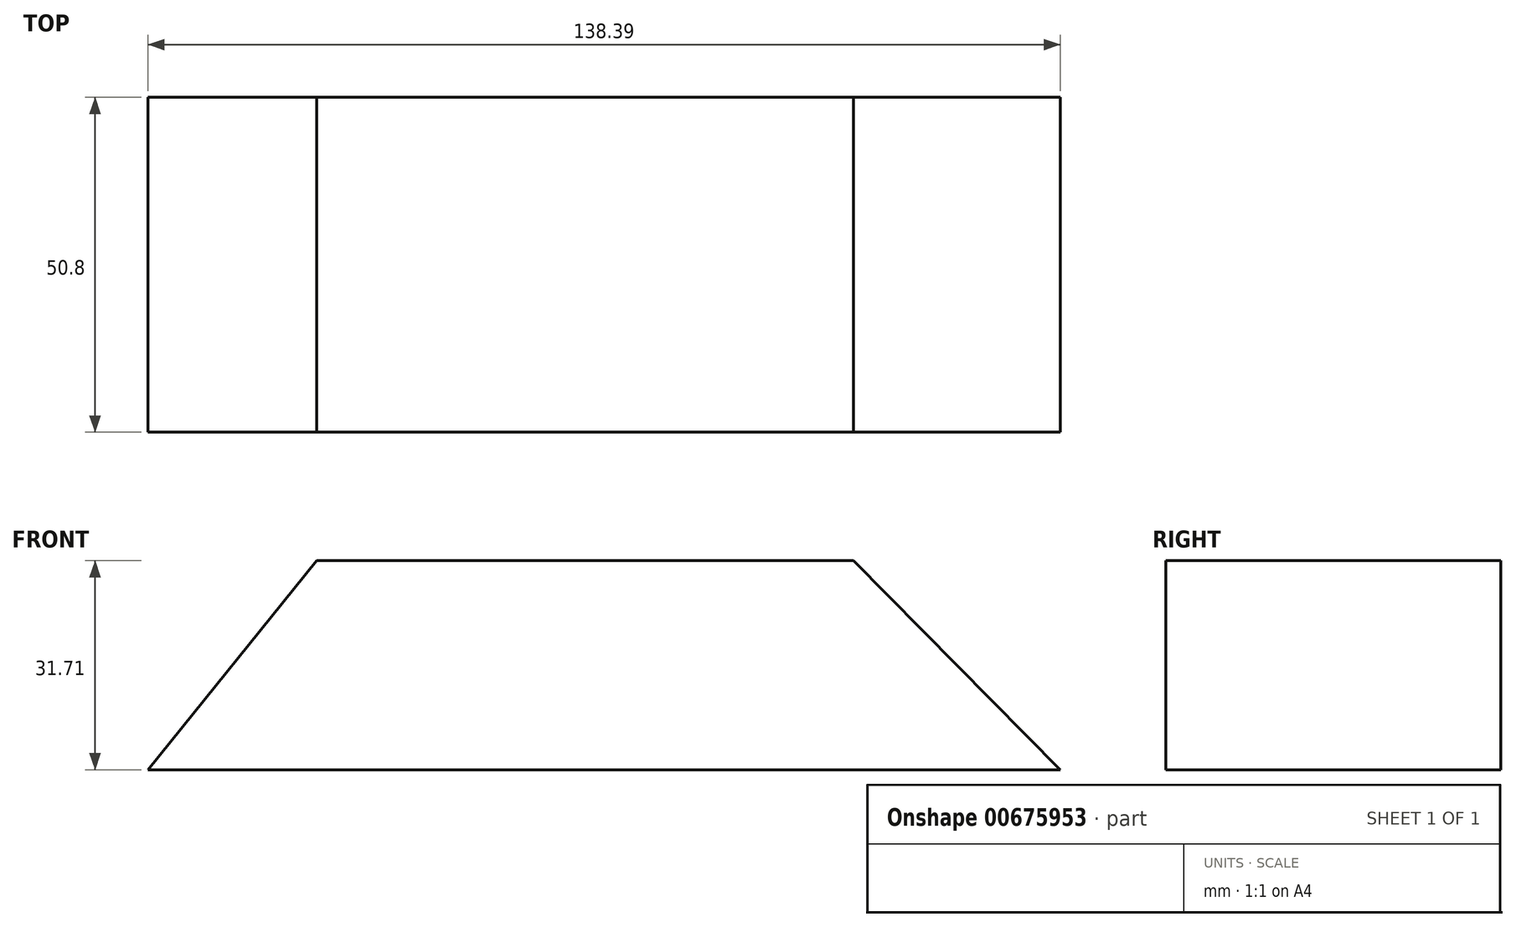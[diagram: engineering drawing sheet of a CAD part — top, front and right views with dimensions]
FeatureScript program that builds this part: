
annotation { "Feature Type Name" : "Feature", "Feature Type Description" : "" }
export const myFeature = defineFeature(function(context is Context, id is Id, definition is map)
    precondition{}
    {
        {
            var Q0;
            Q0=qCreatedBy(makeId("Front.planeOp"),FACE);
            var sketch = newSketch(context, id + "F0", { "sketchPlane" : qUnion([Q0])});
            skLineSegment(sketch, "E0", {"start": v(-63.61, -11.71) * mm, "end": v(74.78, -11.71) * mm});
            skLineSegment(sketch, "E1", {"start": v(74.78, -11.71) * mm, "end": v(43.43, 20) * mm});
            skLineSegment(sketch, "E2", {"start": v(43.43, 20) * mm, "end": v(-38.02, 20) * mm});
            skLineSegment(sketch, "E3", {"start": v(-38.02, 20) * mm, "end": v(-63.61, -11.71) * mm});
            skSolve(sketch);
        }
        {
            var Q0;
            Q0=makeQuery(id+"F0.imprint","IMPRINT",FACE,{"disambiguationData":[TD([[makeQuery(id+"F0.imprint","IMPRINT",EDGE,{"derivedFrom":sQuery(id+"F0.wireOp",EDGE,"E0")}),1.0]])]});
            extrude(context, id + "F1", {"entities" : qUnion([Q0]), "depth" : 50.8 * mm, "offsetDistance" : 25.4 * mm});
        }
    });
